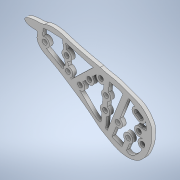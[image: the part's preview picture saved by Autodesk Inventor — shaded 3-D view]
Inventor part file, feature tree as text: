
AUTODESK INVENTOR PART (.ipt)
format: ipt  version: 2022 (Build 260153000, 153)  size: 411,136 bytes
history: native  units: in
note: dims shown in document units (in); Inventor stores cm internally (conversion verified against a paired STEP export)
features: extrude x1, sketch x1
ambient origin geometry x8: Origin, YZ Plane, XZ Plane, XY Plane, X Axis, Y Axis, Z Axis, Center Point
bodies: Body1 (feature_tree)
feature tree (2):
  extrude  "Extrusion1"  TaperAngle=0.0deg  [1 undecoded]
  sketch  "Sketch4"  dims[d0=0.1969in d1=0.0in d2=0.2559in d7=0.7087in d8=0.7087in d9=0.7087in d10=0.7087in d11=0.7087in d13=0.2559in d14=0.2559in d15=0.2559in d16=0.7087in d18=0.2559in d19=0.7087in d20=0.7087in d3=1.9685in]
note: 1 required parameter value undecoded (feature->parameter linkage not recoverable at this tier; creation-order binding heuristic only, values carry confidence <= 0.55)
